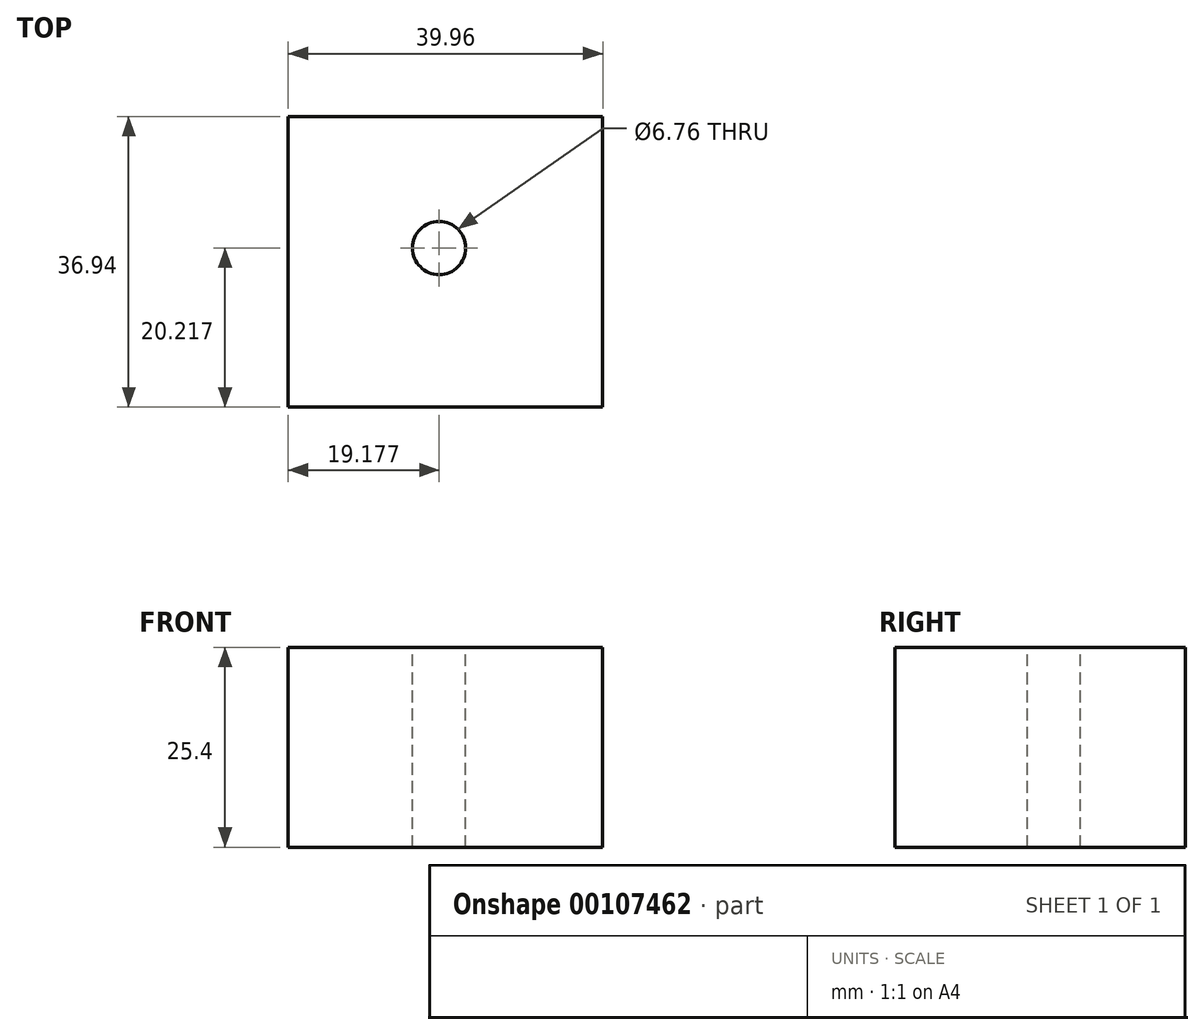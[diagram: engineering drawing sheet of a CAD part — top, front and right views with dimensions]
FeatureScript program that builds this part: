
annotation { "Feature Type Name" : "Feature", "Feature Type Description" : "" }
export const myFeature = defineFeature(function(context is Context, id is Id, definition is map)
    precondition{}
    {
        {
            var Q0;
            Q0=qCreatedBy(makeId("Top.planeOp"),FACE);
            var sketch = newSketch(context, id + "F0", { "sketchPlane" : qUnion([Q0])});
            skLineSegment(sketch, "E0.bottom", {"start": v(0, 0) * mm, "end": v(39.96, 0) * mm});
            skLineSegment(sketch, "E0.top", {"start": v(0, 36.94) * mm, "end": v(39.96, 36.94) * mm});
            skLineSegment(sketch, "E0.left", {"start": v(0, 0) * mm, "end": v(0, 36.94) * mm});
            skLineSegment(sketch, "E0.right", {"start": v(39.96, 0) * mm, "end": v(39.96, 36.94) * mm});
            skSolve(sketch);
        }
        {
            var Q0;
            Q0=makeQuery(id+"F0.imprint","IMPRINT",FACE,{"disambiguationData":[TD([[makeQuery(id+"F0.imprint","IMPRINT",EDGE,{"derivedFrom":sQuery(id+"F0.wireOp",EDGE,"E0.bottom")}),1.0]])]});
            extrude(context, id + "F1", {"entities" : qUnion([Q0]), "depth" : 25.4 * mm});
        }
        {
            var Q0;
            Q0=makeQuery(id+"F1.opExtrude","CAP_FACE",FACE,{"disambiguationData":[OSD([sQuery(id+"F0.wireOp",EDGE,"E0.bottom"),sQuery(id+"F0.wireOp",EDGE,"E0.top"),sQuery(id+"F0.wireOp",EDGE,"E0.left"),sQuery(id+"F0.wireOp",EDGE,"E0.right")])],"isStart":false});
            var sketch = newSketch(context, id + "F2", { "sketchPlane" : qUnion([Q0])});
            skCircle(sketch, "E1", {"center": v(19.18, 20.22) * mm, "radius": 8.2 * mm});
            skSolve(sketch);
        }
        {
            var Q0;
            Q0=sQuery(id+"F2.wireOp",VERTEX,"E1.center");
            var Q1;
            Q1=makeQuery(id+"F1.opExtrude","SWEPT_BODY",BODY,{"disambiguationData":[OSD([sQuery(id+"F0.wireOp",EDGE,"E0.bottom"),sQuery(id+"F0.wireOp",EDGE,"E0.top"),sQuery(id+"F0.wireOp",EDGE,"E0.left"),sQuery(id+"F0.wireOp",EDGE,"E0.right")])]});
            hole(context, id + "F3", {"style" : HoleStyle.SIMPLE, "endStyle" : HoleEndStyle.THROUGH, "standardTappedOrClearance" : lookupTablePath({ "standard" : "ANSI", "fit" : "Normal (ASME)", "size" : "1/4", "type" : "Clearance" }), "standardBlindInLast" : lookupTablePath({ "fit" : "Free", "standard" : "ANSI", "size" : "1/4", "type" : "Clearance" }), "holeDiameter" : 6.76 * mm, "locations" : qUnion([Q0]), "scope" : qUnion([Q1]), "isTappedThrough" : true});
        }
    });
